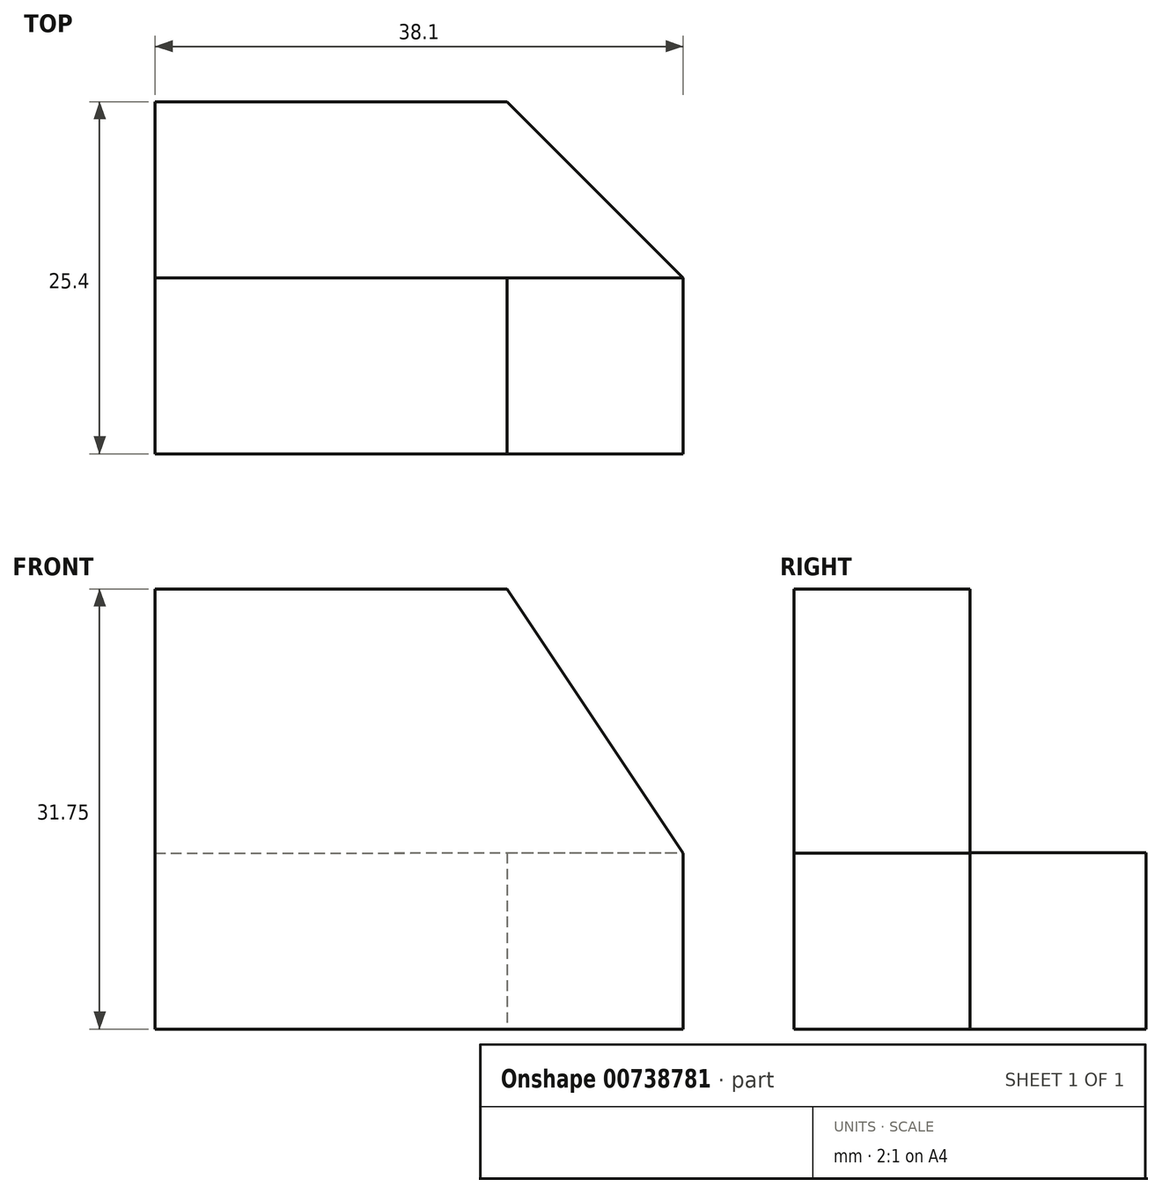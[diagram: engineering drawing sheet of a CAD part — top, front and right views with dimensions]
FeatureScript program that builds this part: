
annotation { "Feature Type Name" : "Feature", "Feature Type Description" : "" }
export const myFeature = defineFeature(function(context is Context, id is Id, definition is map)
    precondition{}
    {
        {
            var Q0;
            Q0=qCreatedBy(makeId("Front.planeOp"),FACE);
            var sketch = newSketch(context, id + "F0", { "sketchPlane" : qUnion([Q0])});
            skLineSegment(sketch, "E0", {"start": v(0, 0) * mm, "end": v(0, 31.75) * mm});
            skLineSegment(sketch, "E1", {"start": v(0, 31.75) * mm, "end": v(38.1, 31.75) * mm});
            skLineSegment(sketch, "E2", {"start": v(38.1, 31.75) * mm, "end": v(38.1, 0) * mm});
            skLineSegment(sketch, "E3", {"start": v(38.1, 0) * mm, "end": v(0, 0) * mm});
            skSolve(sketch);
        }
        {
            var Q0;
            Q0 = qSketchRegion(id + "F0", true);
            extrude(context, id + "F1", {"entities" : qUnion([Q0]), "depth" : 25.4 * mm, "offsetDistance" : 25.4 * mm});
        }
        {
            var Q0;
            Q0=makeQuery(id+"F1.opExtrude","CAP_FACE",FACE,{"disambiguationData":[OSD([sQuery(id+"F0.wireOp",EDGE,"E0"),sQuery(id+"F0.wireOp",EDGE,"E1"),sQuery(id+"F0.wireOp",EDGE,"E2"),sQuery(id+"F0.wireOp",EDGE,"E3")])],"isStart":false});
            var sketch = newSketch(context, id + "F2", { "sketchPlane" : qUnion([Q0])});
            skLineSegment(sketch, "E4", {"start": v(25.4, 31.75) * mm, "end": v(38.1, 12.7) * mm});
            skLineSegment(sketch, "E5", {"start": v(38.1, 12.7) * mm, "end": v(38.1, 31.75) * mm});
            skLineSegment(sketch, "E6", {"start": v(38.1, 31.75) * mm, "end": v(25.4, 31.75) * mm});
            skSolve(sketch);
        }
        {
            var Q0;
            Q0=makeQuery(id+"F2.imprint","IMPRINT",FACE,{"disambiguationData":[TD([[makeQuery(id+"F2.imprint","IMPRINT",EDGE,{"derivedFrom":sQuery(id+"F2.wireOp",EDGE,"E4")}),1.0]])]});
            extrude(context, id + "F3", {"entities" : qUnion([Q0]), "operationType" : NewBodyOperationType.REMOVE, "oppositeDirection" : true, "depth" : 25.4 * mm, "offsetDistance" : 25.4 * mm});
        }
        {
            var Q0;
            Q0=qCreatedBy(makeId("Front.planeOp"),FACE);
            var sketch = newSketch(context, id + "F4", { "sketchPlane" : qUnion([Q0])});
            skLineSegment(sketch, "E7", {"start": v(38.1, 12.7) * mm, "end": v(25.4, 31.75) * mm});
            skLineSegment(sketch, "E8", {"start": v(25.4, 31.75) * mm, "end": v(0, 31.75) * mm});
            skLineSegment(sketch, "E9", {"start": v(0, 31.75) * mm, "end": v(0, 12.7) * mm});
            skLineSegment(sketch, "E10", {"start": v(0, 12.7) * mm, "end": v(38.1, 12.7) * mm});
            skSolve(sketch);
        }
        {
            var Q0;
            Q0 = qSketchRegion(id + "F4", true);
            extrude(context, id + "F5", {"entities" : qUnion([Q0]), "operationType" : NewBodyOperationType.REMOVE, "depth" : 12.7 * mm, "offsetDistance" : 25.4 * mm});
        }
        {
            var Q0;
            Q0=qCreatedBy(makeId("Top.planeOp"),FACE);
            var sketch = newSketch(context, id + "F6", { "sketchPlane" : qUnion([Q0])});
            skLineSegment(sketch, "E11", {"start": v(38.1, -12.7) * mm, "end": v(25.4, 0) * mm});
            skLineSegment(sketch, "E12", {"start": v(25.4, 0) * mm, "end": v(38.1, 0) * mm});
            skLineSegment(sketch, "E13", {"start": v(38.1, 0) * mm, "end": v(38.1, -12.7) * mm});
            skSolve(sketch);
        }
        {
            var Q0;
            Q0 = qSketchRegion(id + "F6", true);
            extrude(context, id + "F7", {"entities" : qUnion([Q0]), "operationType" : NewBodyOperationType.REMOVE, "depth" : 25.4 * mm, "offsetDistance" : 25.4 * mm});
        }
    });
